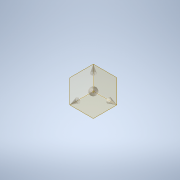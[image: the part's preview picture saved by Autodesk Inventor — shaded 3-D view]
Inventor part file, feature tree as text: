
AUTODESK INVENTOR PART (.ipt)
format: ipt  version: 2022 (Build 260153000, 153)  size: 9,573,888 bytes
history: native  units: mm
features: sketch x9, surface_op x6, plane x3, mirror x2, boolean_combine x2, extrude x2, other x2, loft x1, sweep x1, split x1
ambient origin geometry x8: Origin, YZ Plane, XZ Plane, XY Plane, X Axis, Y Axis, Z Axis, Center Point
bodies: Solid10 (feature_tree), Solid12 (feature_tree), Solid13 (feature_tree)
feature tree (29):
  sketch  "Sketch1"  dims[d3=30.0mm d27=20.0mm]
  sketch  "Sketch2"  dims[d33=7.5mm d34=2.0mm]
  plane  "Work Plane1"
  sketch  "3D Sketch1"
  sketch  "Sketch4"  dims[d35=0.0mm d36=90.0deg d37=0.0mm d38=90.0deg]
  plane  "Work Plane2"
  sketch  "Sketch6"  dims[d39=-7.5mm d42=20.0mm]
  loft  "Loft1"
  plane  "Work Plane3"
  sweep  "Sweep13"
  mirror  "Mirror3"
  mirror  "Mirror4"
  sketch  "Sketch8"  dims[d44=310.0mm]
  boolean_combine  "Combine1"
  extrude  "Extrusion2"  TaperAngle=0.0deg  [1 undecoded]
  boolean_combine  "Combine2"
  surface_op  "Extend4"
  surface_op  "Extend5"
  surface_op  "Extend6"
  surface_op  "Extend7"
  surface_op  "Extend8"
  split  "Split1"
  extrude  "Extrusion4"  Depth=20.0mm
  sketch  "Sketch7"  dims[d43=7.5mm]
  other  "Pattern of Solid10:2"
  sketch  "3D Sketch2"
  other  "Srf1"
  sketch  "Sketch11"  dims[d45=0.0mm d46=0.0mm d47=680.0mm d48=90.0deg d49=50.0mm d51=70.0mm d52=0.0mm d53=0.0mm d62=70.0mm d63=2184.75mm d64=3451.75mm d65=47138.5mm d66=69536.75mm d69=10000.0mm d70=0.0mm d50=0.5mm d54=0.872665mm d71=0.5mm d72=0.872665mm]
  surface_op  "Boundary Patch1"
note: 1 required parameter value undecoded (feature->parameter linkage not recoverable at this tier; creation-order binding heuristic only, values carry confidence <= 0.55)
